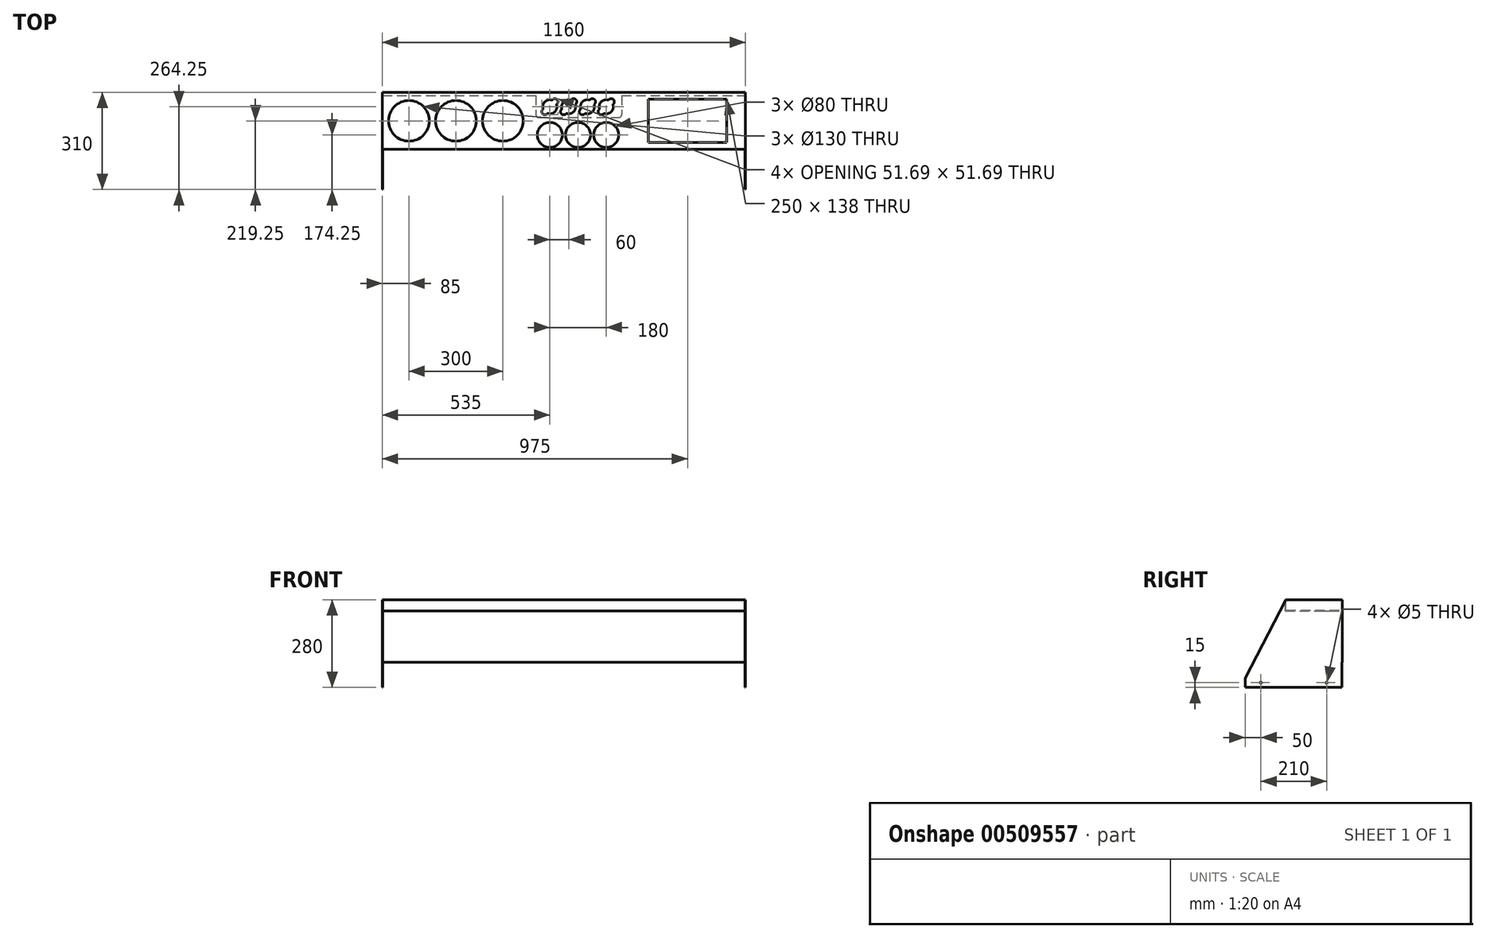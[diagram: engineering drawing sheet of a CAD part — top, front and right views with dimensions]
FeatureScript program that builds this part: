
annotation { "Feature Type Name" : "Feature", "Feature Type Description" : "" }
export const myFeature = defineFeature(function(context is Context, id is Id, definition is map)
    precondition{}
    {
        {
            var Q0;
            Q0=qCreatedBy(makeId("Right.planeOp"),FACE);
            var sketch = newSketch(context, id + "F0", { "sketchPlane" : qUnion([Q0])});
            skLineSegment(sketch, "E0", {"start": v(0, 0) * mm, "end": v(0, 30) * mm});
            skLineSegment(sketch, "E1", {"start": v(0, 30) * mm, "end": v(130, 280) * mm});
            skLineSegment(sketch, "E2", {"start": v(130, 280) * mm, "end": v(310, 280) * mm});
            skLineSegment(sketch, "E3", {"start": v(310, 280) * mm, "end": v(310, 0) * mm});
            skLineSegment(sketch, "E4", {"start": v(310, 0) * mm, "end": v(0, 0) * mm});
            skSolve(sketch);
        }
        {
            var Q0;
            Q0 = qSketchRegion(id + "F0", true);
            extrude(context, id + "F1", {"entities" : qUnion([Q0]), "depth" : 1160 * mm});
        }
        {
            var Q0;
            Q0=makeQuery(id+"F1.opExtrude","SWEPT_FACE",FACE,{"disambiguationData":[OSD([sQuery(id+"F0.wireOp",EDGE,"E1")])]});
            var Q1;
            Q1=makeQuery(id+"F1.opExtrude","SWEPT_FACE",FACE,{"disambiguationData":[OSD([sQuery(id+"F0.wireOp",EDGE,"E2")])]});
            var Q2;
            Q2=makeQuery(id+"F1.opExtrude","SWEPT_FACE",FACE,{"disambiguationData":[OSD([sQuery(id+"F0.wireOp",EDGE,"E0")])]});
            var Q3;
            Q3=makeQuery(id+"F1.opExtrude","SWEPT_FACE",FACE,{"disambiguationData":[OSD([sQuery(id+"F0.wireOp",EDGE,"E4")])]});
            shell(context, id + "F2", {"entities" : qUnion([Q0, Q1, Q2, Q3]), "thickness" : 1.5 * mm});
        }
        {
            var Q0;
            Q0=makeQuery(id+"F2.opShell","OFFSET_FACE",FACE,{"disambiguationData":[OSD([sQuery(id+"F0.wireOp",EDGE,"E3")])]});
            var sketch = newSketch(context, id + "F3", { "sketchPlane" : qUnion([Q0])});
            skLineSegment(sketch, "E5.bottom", {"start": v(1.5, 280) * mm, "end": v(1158.5, 280) * mm});
            skLineSegment(sketch, "E5.top", {"start": v(1.5, 278.5) * mm, "end": v(1158.5, 278.5) * mm});
            skLineSegment(sketch, "E5.left", {"start": v(1.5, 280) * mm, "end": v(1.5, 278.5) * mm});
            skLineSegment(sketch, "E5.right", {"start": v(1158.5, 280) * mm, "end": v(1158.5, 278.5) * mm});
            skSolve(sketch);
        }
        {
            var Q0;
            Q0 = qSketchRegion(id + "F3", true);
            extrude(context, id + "F4", {"entities" : qUnion([Q0]), "operationType" : NewBodyOperationType.ADD, "depth" : 180 * mm, "offsetDistance" : 25 * mm});
        }
        {
            var Q0;
            Q0=makeQuery(id+"F4.opExtrude","SWEPT_FACE",FACE,{"disambiguationData":[OSD([sQuery(id+"F3.wireOp",EDGE,"E5.top")])]});
            var sketch = newSketch(context, id + "F5", { "sketchPlane" : qUnion([Q0])});
            skLineSegment(sketch, "E6.bottom", {"start": v(1.5, -128.5) * mm, "end": v(1158.5, -128.5) * mm});
            skLineSegment(sketch, "E6.top", {"start": v(1.5, -130) * mm, "end": v(1158.5, -130) * mm});
            skLineSegment(sketch, "E6.left", {"start": v(1.5, -128.5) * mm, "end": v(1.5, -130) * mm});
            skLineSegment(sketch, "E6.right", {"start": v(1158.5, -128.5) * mm, "end": v(1158.5, -130) * mm});
            skSolve(sketch);
        }
        {
            var Q0;
            Q0 = qSketchRegion(id + "F5", true);
            extrude(context, id + "F6", {"entities" : qUnion([Q0]), "operationType" : NewBodyOperationType.ADD, "depth" : 35 * mm});
        }
        {
            var Q0;
            Q0=makeQuery(id+"F6.opExtrude","SWEPT_FACE",FACE,{"disambiguationData":[OSD([sQuery(id+"F5.wireOp",EDGE,"E6.top")])]});
            var sketch = newSketch(context, id + "F7", { "sketchPlane" : qUnion([Q0])});
            skLineSegment(sketch, "E7.bottom", {"start": v(-1.5, 243.5) * mm, "end": v(-1158.5, 243.5) * mm});
            skLineSegment(sketch, "E7.top", {"start": v(-1.5, 245) * mm, "end": v(-1158.5, 245) * mm});
            skLineSegment(sketch, "E7.left", {"start": v(-1.5, 243.5) * mm, "end": v(-1.5, 245) * mm});
            skLineSegment(sketch, "E7.right", {"start": v(-1158.5, 243.5) * mm, "end": v(-1158.5, 245) * mm});
            skSolve(sketch);
        }
        {
            var Q0;
            Q0 = qSketchRegion(id + "F7", true);
            extrude(context, id + "F8", {"entities" : qUnion([Q0]), "operationType" : NewBodyOperationType.ADD, "depth" : 170 * mm});
        }
        {
            var Q0;
            Q0=makeQuery(id+"F1.opExtrude","SWEPT_FACE",FACE,{"disambiguationData":[OSD([sQuery(id+"F0.wireOp",EDGE,"E3")])]});
            var sketch = newSketch(context, id + "F9", { "sketchPlane" : qUnion([Q0])});
            skLineSegment(sketch, "E8.bottom", {"start": v(-1160, 0) * mm, "end": v(0, 0) * mm});
            skLineSegment(sketch, "E8.top", {"start": v(-1160, 80) * mm, "end": v(0, 80) * mm});
            skLineSegment(sketch, "E8.left", {"start": v(-1160, 0) * mm, "end": v(-1160, 80) * mm});
            skLineSegment(sketch, "E8.right", {"start": v(0, 0) * mm, "end": v(0, 80) * mm});
            skSolve(sketch);
        }
        {
            var Q0;
            Q0 = qSketchRegion(id + "F9", true);
            extrude(context, id + "F10", {"entities" : qUnion([Q0]), "operationType" : NewBodyOperationType.REMOVE, "oppositeDirection" : true, "depth" : 1.5 * mm});
        }
        {
            var Q0;
            Q0=makeQuery(id+"F4.boolean.opBoolean","MERGE",FACE,{"derivedFrom":[makeQuery(id+"F1.opExtrude","SWEPT_FACE",FACE,{"disambiguationData":[OSD([sQuery(id+"F0.wireOp",EDGE,"E2")])]}),makeQuery(id+"F4.opExtrude","SWEPT_FACE",FACE,{"disambiguationData":[OSD([sQuery(id+"F3.wireOp",EDGE,"E5.bottom")])]})]});
            var sketch = newSketch(context, id + "F11", { "sketchPlane" : qUnion([Q0])});
            skLineSegment(sketch, "E9", {"start": v(-35.48, 219.25) * mm, "end": v(1178.78, 219.25) * mm, "construction": true});
            skCircle(sketch, "E10", {"center": v(85, 219.25) * mm, "radius": 65 * mm});
            skCircle(sketch, "E11", {"center": v(235, 219.25) * mm, "radius": 65 * mm});
            skCircle(sketch, "E12", {"center": v(385, 219.25) * mm, "radius": 65 * mm});
            skLineSegment(sketch, "E13", {"start": v(480.56, 174.25) * mm, "end": v(786.47, 174.25) * mm, "construction": true});
            skCircle(sketch, "E14", {"center": v(535, 174.25) * mm, "radius": 40 * mm});
            skCircle(sketch, "E15", {"center": v(625, 174.25) * mm, "radius": 40 * mm});
            skCircle(sketch, "E16", {"center": v(715, 174.25) * mm, "radius": 40 * mm});
            skLineSegment(sketch, "E17", {"start": v(479.57, 264.25) * mm, "end": v(780.85, 264.25) * mm, "construction": true});
            skArc(sketch, "E18", {"start": v(527.56, 243.02) * mm, "mid": v(550.9, 248.34) * mm, "end": v(556.23, 271.7) * mm});
            skLineSegment(sketch, "E19", {"start": v(508.34, 237.6) * mm, "end": v(563.27, 292.52) * mm, "construction": true});
            skArc(sketch, "E20", {"start": v(513.77, 256.8) * mm, "mid": v(512.02, 241.27) * mm, "end": v(527.56, 243.02) * mm});
            skArc(sketch, "E21", {"start": v(556.23, 271.7) * mm, "mid": v(557.98, 287.23) * mm, "end": v(542.44, 285.48) * mm});
            skArc(sketch, "E22.trimOffspring", {"start": v(542.44, 285.48) * mm, "mid": v(519.1, 280.16) * mm, "end": v(513.77, 256.8) * mm});
            skArc(sketch, "E23.1.0.0", {"start": v(602.44, 285.48) * mm, "mid": v(579.1, 280.16) * mm, "end": v(573.77, 256.8) * mm});
            skArc(sketch, "E23.1.0.1", {"start": v(616.23, 271.7) * mm, "mid": v(617.98, 287.23) * mm, "end": v(602.44, 285.48) * mm});
            skArc(sketch, "E23.1.0.2", {"start": v(587.56, 243.02) * mm, "mid": v(610.9, 248.34) * mm, "end": v(616.23, 271.7) * mm});
            skArc(sketch, "E23.1.0.3", {"start": v(573.77, 256.8) * mm, "mid": v(572.02, 241.27) * mm, "end": v(587.56, 243.02) * mm});
            skArc(sketch, "E23.2.0.0", {"start": v(662.44, 285.48) * mm, "mid": v(639.1, 280.16) * mm, "end": v(633.77, 256.8) * mm});
            skArc(sketch, "E23.2.0.1", {"start": v(676.23, 271.7) * mm, "mid": v(677.98, 287.23) * mm, "end": v(662.44, 285.48) * mm});
            skArc(sketch, "E23.2.0.2", {"start": v(647.56, 243.02) * mm, "mid": v(670.9, 248.34) * mm, "end": v(676.23, 271.7) * mm});
            skArc(sketch, "E23.2.0.3", {"start": v(633.77, 256.8) * mm, "mid": v(632.02, 241.27) * mm, "end": v(647.56, 243.02) * mm});
            skArc(sketch, "E23.3.0.0", {"start": v(722.44, 285.48) * mm, "mid": v(699.1, 280.16) * mm, "end": v(693.77, 256.8) * mm});
            skArc(sketch, "E23.3.0.1", {"start": v(736.23, 271.7) * mm, "mid": v(737.98, 287.23) * mm, "end": v(722.44, 285.48) * mm});
            skArc(sketch, "E23.3.0.2", {"start": v(707.56, 243.02) * mm, "mid": v(730.9, 248.34) * mm, "end": v(736.23, 271.7) * mm});
            skArc(sketch, "E23.3.0.3", {"start": v(693.77, 256.8) * mm, "mid": v(692.02, 241.27) * mm, "end": v(707.56, 243.02) * mm});
            skLineSegment(sketch, "E23.direction1", {"start": v(513.77, 256.8) * mm, "end": v(573.77, 256.8) * mm, "construction": true});
            skLineSegment(sketch, "E24.bottom", {"start": v(1100, 288.25) * mm, "end": v(850, 288.25) * mm});
            skLineSegment(sketch, "E24.top", {"start": v(1100, 150.25) * mm, "end": v(850, 150.25) * mm});
            skLineSegment(sketch, "E24.left", {"start": v(1100, 288.25) * mm, "end": v(1100, 150.25) * mm});
            skLineSegment(sketch, "E24.right", {"start": v(850, 288.25) * mm, "end": v(850, 150.25) * mm});
            skPoint(sketch, "E24.middle", {"position": v(975, 219.25) * mm});
            skSolve(sketch);
        }
        {
            var Q0;
            Q0 = qSketchRegion(id + "F11", true);
            extrude(context, id + "F12", {"entities" : qUnion([Q0]), "operationType" : NewBodyOperationType.REMOVE, "endBound" : BoundingType.UP_TO_NEXT, "oppositeDirection" : true, "depth" : 25 * mm});
        }
        {
            var Q0;
            Q0=makeQuery(id+"F8.opExtrude","SWEPT_FACE",FACE,{"disambiguationData":[OSD([sQuery(id+"F7.wireOp",EDGE,"E7.top")])]});
            var sketch = newSketch(context, id + "F13", { "sketchPlane" : qUnion([Q0])});
            skLineSegment(sketch, "E25.bottom", {"start": v(490, 300) * mm, "end": v(765, 300) * mm});
            skLineSegment(sketch, "E25.top", {"start": v(500, 230) * mm, "end": v(755, 230) * mm});
            skLineSegment(sketch, "E25.left", {"start": v(490, 300) * mm, "end": v(490, 240) * mm});
            skLineSegment(sketch, "E25.right", {"start": v(765, 300) * mm, "end": v(765, 240) * mm});
            skPoint(sketch, "E26.visualSharp", {"position": v(490, 230) * mm});
            skArc(sketch, "E26.filletArc", {"start": v(490, 240) * mm, "mid": v(492.93, 232.93) * mm, "end": v(500, 230) * mm});
            skPoint(sketch, "E27.visualSharp", {"position": v(765, 230) * mm});
            skArc(sketch, "E27.filletArc", {"start": v(755, 230) * mm, "mid": v(762.07, 232.93) * mm, "end": v(765, 240) * mm});
            skSolve(sketch);
        }
        {
            var Q0;
            Q0 = qSketchRegion(id + "F13", true);
            extrude(context, id + "F14", {"entities" : qUnion([Q0]), "operationType" : NewBodyOperationType.REMOVE, "endBound" : BoundingType.THROUGH_ALL, "oppositeDirection" : true, "depth" : 25 * mm});
        }
        {
            var Q0;
            Q0=makeQuery(id+"F1.opExtrude","CAP_FACE",FACE,{"disambiguationData":[OSD([sQuery(id+"F0.wireOp",EDGE,"E0"),sQuery(id+"F0.wireOp",EDGE,"E1"),sQuery(id+"F0.wireOp",EDGE,"E2"),sQuery(id+"F0.wireOp",EDGE,"E3"),sQuery(id+"F0.wireOp",EDGE,"E4")])],"isStart":false});
            var sketch = newSketch(context, id + "F15", { "sketchPlane" : qUnion([Q0])});
            skLineSegment(sketch, "E28", {"start": v(292.37, 15) * mm, "end": v(8.62, 15) * mm, "construction": true});
            skCircle(sketch, "E29", {"center": v(260, 15) * mm, "radius": 2.5 * mm});
            skCircle(sketch, "E30", {"center": v(50, 15) * mm, "radius": 2.5 * mm});
            skSolve(sketch);
        }
        {
            var Q0;
            Q0 = qSketchRegion(id + "F15", true);
            extrude(context, id + "F16", {"entities" : qUnion([Q0]), "operationType" : NewBodyOperationType.REMOVE, "endBound" : BoundingType.THROUGH_ALL, "oppositeDirection" : true, "depth" : 25 * mm, "offsetDistance" : 25 * mm});
        }
    });
